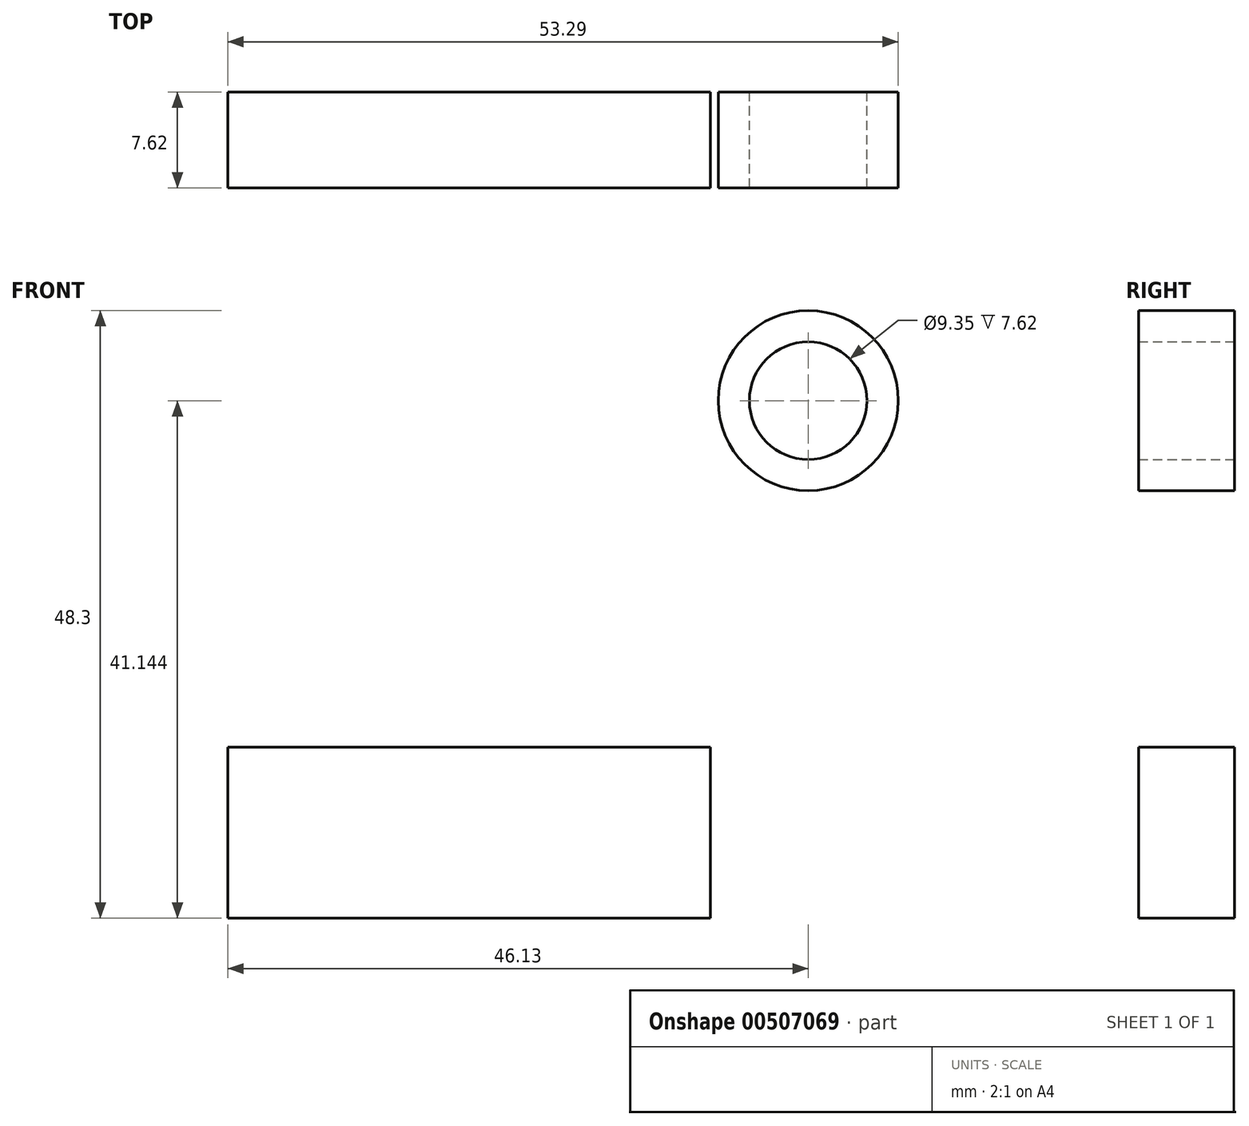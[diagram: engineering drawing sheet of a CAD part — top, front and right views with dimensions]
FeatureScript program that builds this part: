
annotation { "Feature Type Name" : "Feature", "Feature Type Description" : "" }
export const myFeature = defineFeature(function(context is Context, id is Id, definition is map)
    precondition{}
    {
        {
            var Q0;
            Q0=qCreatedBy(makeId("Front.planeOp"),FACE);
            var sketch = newSketch(context, id + "F0", { "sketchPlane" : qUnion([Q0])});
            skLineSegment(sketch, "E0.bottom", {"start": v(-7.79, 62.05) * mm, "end": v(7.79, 62.05) * mm, "construction": true});
            skLineSegment(sketch, "E0.top", {"start": v(-7.79, -62.05) * mm, "end": v(7.79, -62.05) * mm, "construction": true});
            skLineSegment(sketch, "E0.left", {"start": v(-7.79, 62.05) * mm, "end": v(-7.79, -62.05) * mm});
            skLineSegment(sketch, "E0.right", {"start": v(7.79, 62.05) * mm, "end": v(7.79, -62.05) * mm, "construction": true});
            skPoint(sketch, "E0.middle", {"position": v(0, 0) * mm});
            skLineSegment(sketch, "E1.bottom", {"start": v(-46.13, 34.5) * mm, "end": v(46.13, 34.5) * mm});
            skLineSegment(sketch, "E1.top", {"start": v(-46.13, 20.9) * mm, "end": v(46.13, 20.9) * mm});
            skLineSegment(sketch, "E1.left", {"start": v(-46.13, 34.5) * mm, "end": v(-46.13, 20.9) * mm});
            skLineSegment(sketch, "E1.right", {"start": v(46.13, 34.5) * mm, "end": v(46.13, 20.9) * mm, "construction": true});
            skPoint(sketch, "E1.middle", {"position": v(0, 27.7) * mm});
            skCircle(sketch, "E2", {"center": v(0, 62.05) * mm, "radius": 7.16 * mm});
            skCircle(sketch, "E3", {"center": v(0, 62.05) * mm, "radius": 4.67 * mm});
            skSolve(sketch);
        }
        {
            var Q0;
            Q0 = qSketchRegion(id + "F0", true);
            extrude(context, id + "F1", {"entities" : qUnion([Q0]), "depth" : 7.62 * mm});
        }
    });
